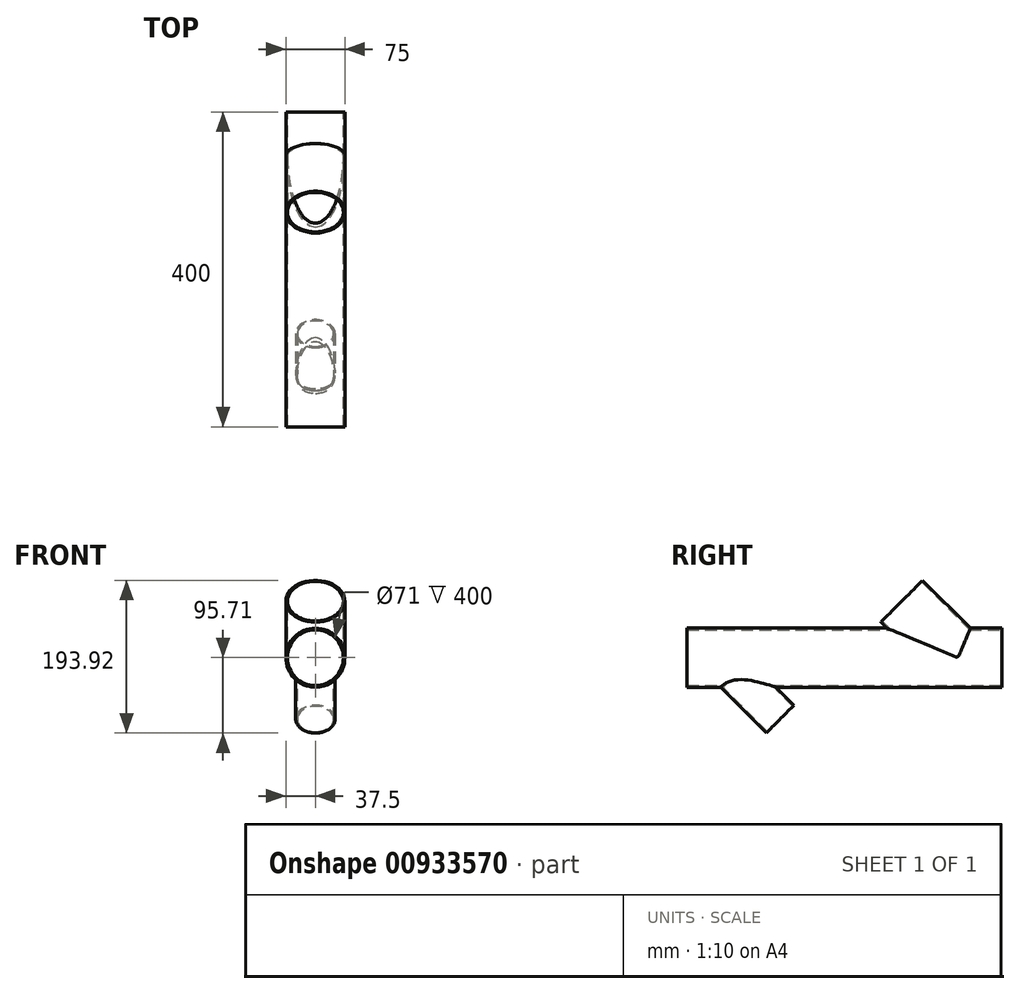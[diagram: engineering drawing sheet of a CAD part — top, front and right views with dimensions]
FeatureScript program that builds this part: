
annotation { "Feature Type Name" : "Feature", "Feature Type Description" : "" }
export const myFeature = defineFeature(function(context is Context, id is Id, definition is map)
    precondition{}
    {
        {
            var Q0;
            Q0=qCreatedBy(makeId("Front.planeOp"),FACE);
            var sketch = newSketch(context, id + "F0", { "sketchPlane" : qUnion([Q0])});
            skCircle(sketch, "E0", {"center": v(0, 0) * mm, "radius": 35.5 * mm});
            skCircle(sketch, "E1", {"center": v(0, 0) * mm, "radius": 37.5 * mm});
            skSolve(sketch);
        }
        {
            var Q0;
            Q0 = qSketchRegion(id + "F0", true);
            extrude(context, id + "F1", {"entities" : qUnion([Q0]), "depth" : 400 * mm, "offsetDistance" : 25 * mm});
        }
        {
            var Q0;
            Q0=qCreatedBy(makeId("Right.planeOp"),FACE);
            var sketch = newSketch(context, id + "F2", { "sketchPlane" : qUnion([Q0])});
            skLineSegment(sketch, "E2", {"start": v(-30, 27.5) * mm, "end": v(-100.71, 98.21) * mm});
            skLineSegment(sketch, "E3", {"start": v(-100.71, 98.21) * mm, "end": v(-102.12, 96.8) * mm});
            skLineSegment(sketch, "E4", {"start": v(-102.12, 96.8) * mm, "end": v(-31.41, 26.09) * mm});
            skLineSegment(sketch, "E5", {"start": v(-97.77, 42.24) * mm, "end": v(-29.63, -25.9) * mm, "construction": true});
            skLineSegment(sketch, "E6", {"start": v(-30, 27.5) * mm, "end": v(-31.41, 26.09) * mm});
            skSolve(sketch);
        }
        {
            var Q0;
            Q0 = qSketchRegion(id + "F2", true);
            var Q1;
            Q1=sQuery(id+"F2.wireOp",EDGE,"E5");
            revolve(context, id + "F3", {"operationType" : NewBodyOperationType.ADD, "surfaceOperationType" : NewSurfaceOperationType.NEW, "entities" : qUnion([Q0]), "axis" : qUnion([Q1]), "revolveType" : RevolveType.FULL});
        }
        {
            var Q0;
            Q0=qCreatedBy(makeId("Right.planeOp"),FACE);
            var sketch = newSketch(context, id + "F4", { "sketchPlane" : qUnion([Q0])});
            skLineSegment(sketch, "E7", {"start": v(-370, -25) * mm, "end": v(-299.29, -95.71) * mm});
            skLineSegment(sketch, "E8", {"start": v(-299.29, -95.71) * mm, "end": v(-297.88, -94.3) * mm});
            skLineSegment(sketch, "E9", {"start": v(-297.88, -94.3) * mm, "end": v(-368.59, -23.59) * mm});
            skLineSegment(sketch, "E10", {"start": v(-368.59, -23.59) * mm, "end": v(-370, -25) * mm});
            skLineSegment(sketch, "E11", {"start": v(-359.64, 0) * mm, "end": v(-263.67, -95.97) * mm, "construction": true});
            skSolve(sketch);
        }
        {
            var Q0;
            Q0 = qSketchRegion(id + "F4", true);
            var Q1;
            Q1=sQuery(id+"F4.wireOp",EDGE,"E11");
            revolve(context, id + "F5", {"operationType" : NewBodyOperationType.ADD, "surfaceOperationType" : NewSurfaceOperationType.NEW, "entities" : qUnion([Q0]), "axis" : qUnion([Q1]), "revolveType" : RevolveType.FULL});
        }
        {
            var Q0;
            Q0=qCreatedBy(makeId("Front.planeOp"),FACE);
            var sketch = newSketch(context, id + "F6", { "sketchPlane" : qUnion([Q0])});
            skCircle(sketch, "E12", {"center": v(0, 0) * mm, "radius": 35.5 * mm});
            skSolve(sketch);
        }
        {
            var Q0;
            Q0 = qSketchRegion(id + "F6", true);
            extrude(context, id + "F7", {"entities" : qUnion([Q0]), "operationType" : NewBodyOperationType.REMOVE, "endBound" : BoundingType.THROUGH_ALL, "depth" : 25 * mm, "offsetDistance" : 25 * mm});
        }
        {
            var Q0;
            Q0=makeQuery(id+"F3.opRevolve","SWEPT_FACE",FACE,{"disambiguationData":[OSD([sQuery(id+"F2.wireOp",EDGE,"E3")])]});
            var sketch = newSketch(context, id + "F8", { "sketchPlane" : qUnion([Q0])});
            skCircle(sketch, "E13", {"center": v(0, -39.27) * mm, "radius": 35.5 * mm});
            skSolve(sketch);
        }
        {
            var Q0;
            Q0 = qSketchRegion(id + "F8", true);
            extrude(context, id + "F9", {"entities" : qUnion([Q0]), "operationType" : NewBodyOperationType.REMOVE, "oppositeDirection" : true, "depth" : 100 * mm, "offsetDistance" : 25 * mm});
        }
        {
            var Q0;
            Q0=makeQuery(id+"F5.opRevolve","SWEPT_FACE",FACE,{"disambiguationData":[OSD([sQuery(id+"F4.wireOp",EDGE,"E8")])]});
            var sketch = newSketch(context, id + "F10", { "sketchPlane" : qUnion([Q0])});
            skCircle(sketch, "E14", {"center": v(0, -254.3) * mm, "radius": 23 * mm});
            skSolve(sketch);
        }
        {
            var Q0;
            Q0 = qSketchRegion(id + "F10", true);
            extrude(context, id + "F11", {"entities" : qUnion([Q0]), "operationType" : NewBodyOperationType.REMOVE, "oppositeDirection" : true, "depth" : 80 * mm, "offsetDistance" : 25 * mm});
        }
    });
